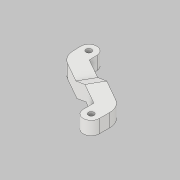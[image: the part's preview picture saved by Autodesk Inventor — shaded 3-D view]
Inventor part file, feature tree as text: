
AUTODESK INVENTOR PART (.ipt)
format: ipt  version: 2019.2 (Build 232265000, 265)  size: 356,864 bytes
history: native  units: mm
features: extrude x5, sketch x5, chamfer x2, fillet x1
ambient origin geometry x8: Origin, YZ Plane, XZ Plane, XY Plane, X Axis, Y Axis, Z Axis, Center Point
bodies: Body1 (feature_tree)
feature tree (13):
  extrude  "Extrusion4"  Depth=3.0mm
  extrude  "Extrusion5"  Depth=5.0mm
  extrude  "Extrusion6"  Depth=5.0mm TaperAngle=0.0deg
  extrude  "Extrusion7"  Depth=5.0mm TaperAngle=0.0deg
  extrude  "Extrusion8"  Depth=5.0mm TaperAngle=0.0deg
  chamfer  "Fase2"  Distance=5.0mm
  chamfer  "Fase3"  Distance=5.0mm
  fillet  "Rundung2"  Radius=5.0mm
  sketch  "Skizze4"  dims[d15=4.0mm d16=3.0mm]
  sketch  "Skizze5"  dims[d17=5.0mm d18=35.0mm]
  sketch  "Skizze6"  dims[d19=5.0mm d20=5.0mm d21=0.0mm]
  sketch  "Skizze7"  dims[d22=10.0mm d23=0.0mm d24=5.0mm d25=0.0mm]
  sketch  "Skizze8"  dims[d26=2.1mm d27=5.0mm d28=0.0mm d33=5.0mm d34=0.0mm d35=5.0mm d36=0.0mm d38=9.0mm d39=5.0mm d40=45.0deg d41=9.0mm d42=5.0mm d43=45.0deg d44=0.25mm d45=4.0mm d46=3.0mm d47=2.1mm]
